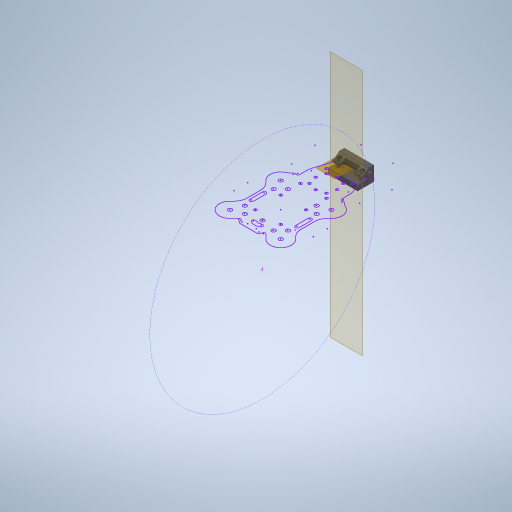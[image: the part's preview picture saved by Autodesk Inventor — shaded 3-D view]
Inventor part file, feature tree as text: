
AUTODESK INVENTOR PART (.ipt)
format: ipt  version: 2023 (Build 270158000, 158)  size: 808,448 bytes
history: native  units: in
note: dims shown in document units (in); Inventor stores cm internally (conversion verified against a paired STEP export)
features: sketch x20, extrude x17, projected_geometry x9, plane x7
ambient origin geometry x8: Origin, YZ Plane, XZ Plane, XY Plane, X Axis, Y Axis, Z Axis, Center Point
bodies: Solid2 (feature_tree)
feature tree (53):
  plane  "Work Plane1"
  plane  "Work Plane7"
  plane  "Work Plane4"
  plane  "Work Plane9"
  sketch  "Sketch13"  dims[d22=0.1181in d23=0.0in d24=0.2008in]
  plane  "Work Plane11"
  extrude  "Extrusion10"  Depth=0.2008in
  plane  "Work Plane8"
  sketch  "Sketch15"  dims[d35=0.0001in d36=1.378in d37=0.0in]
  extrude  "Extrusion12"  Depth=1.378in TaperAngle=0.0deg
  extrude  "Extrusion13"  Depth=1.378in TaperAngle=0.0deg
  extrude  "Extrusion14"  Depth=0.2244in
  extrude  "Extrusion15"  Depth=1.378in TaperAngle=0.0deg
  sketch  "Sketch20"  dims[d47=0.1181in d48=0.1181in d49=0.0in]
  extrude  "Extrusion16"  Depth=0.1181in
  extrude  "Extrusion17"  Depth=0.1181in TaperAngle=0.0deg
  extrude  "Extrusion18"  Depth=0.0394in TaperAngle=0.0deg
  extrude  "Extrusion19"  Depth=0.0394in TaperAngle=0.0deg
  extrude  "Extrusion20"  Depth=0.1575in TaperAngle=0.0deg
  extrude  "Extrusion21"  Depth=0.0787in TaperAngle=0.0deg
  extrude  "Extrusion22"  [1 undecoded]
  extrude  "Extrusion23"  Depth=0.0787in
  extrude  "Extrusion24"  Depth=0.1378in TaperAngle=0.0deg
  extrude  "Extrusion25"  Depth=1.9685in
  plane  "Work Plane12"
  extrude  "Extrusion26"  Depth=1.9685in
  extrude  "Extrusion27"  Depth=1.9685in
  sketch  "Sketch32"  dims[d14=1.9685in]
  sketch  "Sketch33"  dims[d34=0.0197in]
  sketch  "Sketch14"  dims[d25=0.2008in d32=1.378in d33=0.0in]
  sketch  "Sketch17"  dims[d38=0.0in d39=0.0in d40=0.2244in]
  sketch  "Sketch18"  dims[d41=0.2244in d42=1.378in d43=0.0in]
  projected_geometry  "Projected Loop7"
  projected_geometry  "Projected Loop8"
  sketch  "Sketch19"  dims[d44=0.1181in d45=0.0in d46=0.1181in]
  sketch  "Sketch21"  dims[d50=0.0394in d51=0.0in d52=0.0394in d53=0.0in]
  sketch  "Sketch22"  dims[d60=0.0118in d61=0.0394in d62=0.0in]
  projected_geometry  "Projected Loop9"
  sketch  "Sketch23"  dims[d63=0.1575in d64=0.0in d65=0.2963in d66=0.0in]
  projected_geometry  "Projected Loop10"
  projected_geometry  "Projected Loop11"
  sketch  "Sketch24"  dims[d67=0.0787in d68=0.0in d69=0.0787in d70=0.0in]
  sketch  "Sketch25"  dims[d71=0.3937in d72=0.0in d73=-3.0625in]
  projected_geometry  "Projected Loop12"
  sketch  "Sketch26"  dims[d74=0.0787in d75=0.0787in]
  projected_geometry  "Projected Loop13"
  sketch  "Sketch27"  dims[d76=0.2938in d77=0.0in d78=0.1378in d79=0.0in]
  projected_geometry  "Projected Loop14"
  sketch  "Sketch28"  dims[d2=0.0197in d3=1.9685in]
  projected_geometry  "Projected Loop15"
  sketch  "Sketch29"  dims[d4=0.0197in d5=1.9685in]
  sketch  "Sketch30"  dims[d11=0.0197in d12=1.9685in]
  sketch  "Sketch31"  dims[d13=0.0197in]
note: 1 required parameter value undecoded (feature->parameter linkage not recoverable at this tier; creation-order binding heuristic only, values carry confidence <= 0.55)
